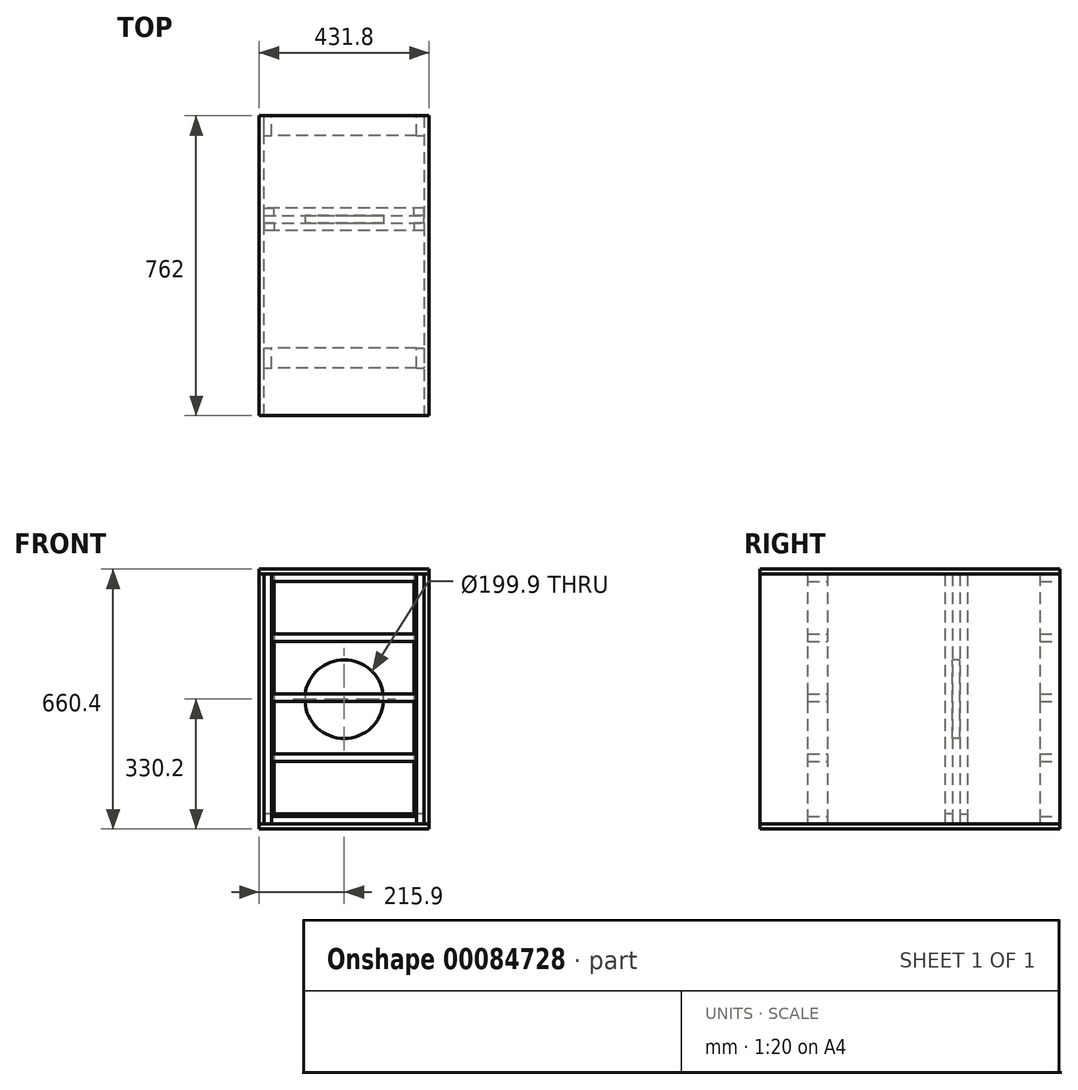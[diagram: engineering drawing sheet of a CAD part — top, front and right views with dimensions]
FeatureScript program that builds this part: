
annotation { "Feature Type Name" : "Feature", "Feature Type Description" : "" }
export const myFeature = defineFeature(function(context is Context, id is Id, definition is map)
    precondition{}
    {
        {
            var Q0;
            Q0=qCreatedBy(makeId("Front.planeOp"),FACE);
            var sketch = newSketch(context, id + "F0", { "sketchPlane" : qUnion([Q0])});
            skLineSegment(sketch, "E0.bottom", {"start": v(-203.2, 317.5) * mm, "end": v(203.2, 317.5) * mm});
            skLineSegment(sketch, "E0.top", {"start": v(-203.2, -317.5) * mm, "end": v(203.2, -317.5) * mm});
            skLineSegment(sketch, "E0.left", {"start": v(-203.2, 317.5) * mm, "end": v(-203.2, -317.5) * mm});
            skLineSegment(sketch, "E0.right", {"start": v(203.2, 317.5) * mm, "end": v(203.2, -317.5) * mm});
            skSolve(sketch);
        }
        {
            var Q0;
            Q0=makeQuery(id+"F0.imprint","IMPRINT",FACE,{"disambiguationData":[TD([[makeQuery(id+"F0.imprint","IMPRINT",EDGE,{"derivedFrom":sQuery(id+"F0.wireOp",EDGE,"E0.bottom")}),-1.0]])]});
            extrude(context, id + "F1", {"entities" : qUnion([Q0]), "depth" : 19.05 * mm});
        }
        {
            var Q0;
            Q0=makeQuery(id+"F1.opExtrude","CAP_FACE",FACE,{"disambiguationData":[OSD([sQuery(id+"F0.wireOp",EDGE,"E0.bottom"),sQuery(id+"F0.wireOp",EDGE,"E0.top"),sQuery(id+"F0.wireOp",EDGE,"E0.left"),sQuery(id+"F0.wireOp",EDGE,"E0.right")])],"isStart":false});
            var sketch = newSketch(context, id + "F2", { "sketchPlane" : qUnion([Q0])});
            skCircle(sketch, "E1", {"center": v(0, 0) * mm, "radius": 166.5 * mm});
            skSolve(sketch);
        }
        {
            var Q0;
            Q0=makeQuery(id+"F2.imprint","IMPRINT",FACE,{"disambiguationData":[TD([[makeQuery(id+"F2.imprint","IMPRINT",EDGE,{"derivedFrom":sQuery(id+"F2.wireOp",EDGE,"E1")}),-1.0]])]});
            var sketch = newSketch(context, id + "F3", { "sketchPlane" : qUnion([Q0])});
            skCircle(sketch, "E2", {"center": v(0, 0) * mm, "radius": 99.95 * mm});
            skSolve(sketch);
        }
        {
            var Q0;
            Q0=makeQuery(id+"F3.imprint","IMPRINT",FACE,{"disambiguationData":[TD([[makeQuery(id+"F3.imprint","IMPRINT",EDGE,{"derivedFrom":sQuery(id+"F3.wireOp",EDGE,"E2")}),1.0]])]});
            extrude(context, id + "F4", {"entities" : qUnion([Q0]), "operationType" : NewBodyOperationType.REMOVE, "endBound" : BoundingType.UP_TO_NEXT, "oppositeDirection" : true, "depth" : 25.4 * mm});
        }
        {
            var Q0;
            Q0=makeQuery(id+"F1.opExtrude","SWEPT_FACE",FACE,{"disambiguationData":[OSD([sQuery(id+"F0.wireOp",EDGE,"E0.top")])]});
            var sketch = newSketch(context, id + "F5", { "sketchPlane" : qUnion([Q0])});
            skLineSegment(sketch, "E3.bottom", {"start": v(203.2, -254) * mm, "end": v(215.9, -254) * mm});
            skLineSegment(sketch, "E3.top", {"start": v(203.2, 508) * mm, "end": v(215.9, 508) * mm});
            skLineSegment(sketch, "E3.left", {"start": v(203.2, -254) * mm, "end": v(203.2, 508) * mm});
            skLineSegment(sketch, "E3.right", {"start": v(215.9, -254) * mm, "end": v(215.9, 508) * mm});
            skLineSegment(sketch, "E4.bottom", {"start": v(-215.9, 508) * mm, "end": v(-203.2, 508) * mm});
            skLineSegment(sketch, "E4.top", {"start": v(-215.9, -254) * mm, "end": v(-203.2, -254) * mm});
            skLineSegment(sketch, "E4.left", {"start": v(-215.9, 508) * mm, "end": v(-215.9, -254) * mm});
            skLineSegment(sketch, "E4.right", {"start": v(-203.2, 508) * mm, "end": v(-203.2, -254) * mm});
            skSolve(sketch);
        }
        {
            var Q0;
            {var subQ3=sQuery(id+"F5.wireOp",EDGE,"E4.bottom");Q0=makeQuery(id+"F5.imprint","IMPRINT",FACE,{"disambiguationData":[TD([[makeQuery(id+"F5.imprint","IMPRINT",EDGE,{"derivedFrom":subQ3}),-1.0]])]});}
            var Q1;
            {var subQ4=sQuery(id+"F5.wireOp",EDGE,"E3.bottom");Q1=makeQuery(id+"F5.imprint","IMPRINT",FACE,{"disambiguationData":[TD([[makeQuery(id+"F5.imprint","IMPRINT",EDGE,{"derivedFrom":subQ4}),1.0]])]});}
            var Q2;
            Q2=makeQuery(id+"F1.opExtrude","SWEPT_FACE",FACE,{"disambiguationData":[OSD([sQuery(id+"F0.wireOp",EDGE,"E0.bottom")])]});
            extrude(context, id + "F6", {"entities" : qUnion([Q0, Q1]), "endBound" : BoundingType.UP_TO_SURFACE, "oppositeDirection" : true, "endBoundEntityFace" : qUnion([Q2]), "depth" : 19.05 * mm});
        }
        {
            var Q0;
            Q0=makeQuery(id+"F1.opExtrude","SWEPT_FACE",FACE,{"disambiguationData":[OSD([sQuery(id+"F0.wireOp",EDGE,"E0.top")])]});
            var sketch = newSketch(context, id + "F7", { "sketchPlane" : qUnion([Q0])});
            skLineSegment(sketch, "E5.bottom", {"start": v(-215.9, 508) * mm, "end": v(215.9, 508) * mm});
            skLineSegment(sketch, "E5.top", {"start": v(-215.9, -254) * mm, "end": v(215.9, -254) * mm});
            skLineSegment(sketch, "E5.left", {"start": v(-215.9, 508) * mm, "end": v(-215.9, -254) * mm});
            skLineSegment(sketch, "E5.right", {"start": v(215.9, 508) * mm, "end": v(215.9, -254) * mm});
            skSolve(sketch);
        }
        {
            var Q0;
            Q0=makeQuery(id+"F7.imprint","IMPRINT",FACE,{"disambiguationData":[TD([[makeQuery(id+"F7.imprint","IMPRINT",EDGE,{"derivedFrom":sQuery(id+"F7.wireOp",EDGE,"E5.bottom")}),-1.0]])]});
            var Q1;
            {var subQ0=sQuery(id+"F0.wireOp",EDGE,"E0.top");Q1=makeQuery(id+"F7.imprint","IMPRINT",FACE,{"disambiguationData":[TD([[makeQuery(id+"F7.imprint","IMPRINT",EDGE,{"derivedFrom":makeQuery(id+"F1.opExtrude","CAP_EDGE",EDGE,{"disambiguationData":[OSD([subQ0])],"isStart":true})}),1.0]])]});}
            extrude(context, id + "F8", {"entities" : qUnion([Q0, Q1]), "depth" : 12.7 * mm});
        }
        {
            var Q0;
            Q0=makeQuery(id+"F8.opExtrude","CAP_FACE",FACE,{"disambiguationData":[OSD([sQuery(id+"F7.wireOp",EDGE,"E5.bottom"),sQuery(id+"F7.wireOp",EDGE,"E5.top"),sQuery(id+"F7.wireOp",EDGE,"E5.left"),sQuery(id+"F7.wireOp",EDGE,"E5.right")])],"isStart":true});
            var sketch = newSketch(context, id + "F9", { "sketchPlane" : qUnion([Q0])});
            skLineSegment(sketch, "E6.bottom", {"start": v(-203.2, -387.35) * mm, "end": v(-184.15, -387.35) * mm});
            skLineSegment(sketch, "E6.top", {"start": v(-203.2, -336.55) * mm, "end": v(-184.15, -336.55) * mm});
            skLineSegment(sketch, "E6.left", {"start": v(-203.2, -387.35) * mm, "end": v(-203.2, -336.55) * mm});
            skLineSegment(sketch, "E6.right", {"start": v(-184.15, -387.35) * mm, "end": v(-184.15, -336.55) * mm});
            skLineSegment(sketch, "E7.bottom", {"start": v(184.15, -336.55) * mm, "end": v(203.2, -336.55) * mm});
            skLineSegment(sketch, "E7.top", {"start": v(184.15, -387.35) * mm, "end": v(203.2, -387.35) * mm});
            skLineSegment(sketch, "E7.left", {"start": v(184.15, -336.55) * mm, "end": v(184.15, -387.35) * mm});
            skLineSegment(sketch, "E7.right", {"start": v(203.2, -336.55) * mm, "end": v(203.2, -387.35) * mm});
            skSolve(sketch);
        }
        {
            var Q0;
            Q0=makeQuery(id+"F9.imprint","IMPRINT",FACE,{"disambiguationData":[TD([[makeQuery(id+"F9.imprint","IMPRINT",EDGE,{"derivedFrom":sQuery(id+"F9.wireOp",EDGE,"E6.bottom")}),1.0]])]});
            var Q1;
            Q1=makeQuery(id+"F9.imprint","IMPRINT",FACE,{"disambiguationData":[TD([[makeQuery(id+"F9.imprint","IMPRINT",EDGE,{"derivedFrom":sQuery(id+"F9.wireOp",EDGE,"E7.bottom")}),-1.0]])]});
            var Q2;
            Q2=makeQuery(id+"F6.opExtrude","CAP_FACE",FACE,{"disambiguationData":[OSD([sQuery(id+"F5.wireOp",EDGE,"E3.bottom"),sQuery(id+"F5.wireOp",EDGE,"E3.top"),sQuery(id+"F5.wireOp",EDGE,"E3.left"),sQuery(id+"F5.wireOp",EDGE,"E3.right")])],"isStart":false});
            extrude(context, id + "F10", {"entities" : qUnion([Q0, Q1]), "endBound" : BoundingType.UP_TO_SURFACE, "endBoundEntityFace" : qUnion([Q2]), "depth" : 19.05 * mm});
        }
        {
            var Q0;
            Q0=makeQuery(id+"F10.opExtrude","SWEPT_FACE",FACE,{"disambiguationData":[OSD([sQuery(id+"F9.wireOp",EDGE,"E6.right")])]});
            var sketch = newSketch(context, id + "F11", { "sketchPlane" : qUnion([Q0])});
            skLineSegment(sketch, "E8.bottom", {"start": v(-387.35, 317.5) * mm, "end": v(-336.55, 317.5) * mm});
            skLineSegment(sketch, "E8.top", {"start": v(-387.35, 298.45) * mm, "end": v(-336.55, 298.45) * mm});
            skLineSegment(sketch, "E8.left", {"start": v(-387.35, 317.5) * mm, "end": v(-387.35, 298.45) * mm});
            skLineSegment(sketch, "E8.right", {"start": v(-336.55, 317.5) * mm, "end": v(-336.55, 298.45) * mm});
            skLineSegment(sketch, "E9.bottom", {"start": v(-387.35, -298.45) * mm, "end": v(-336.55, -298.45) * mm});
            skLineSegment(sketch, "E9.top", {"start": v(-387.35, -317.5) * mm, "end": v(-336.55, -317.5) * mm});
            skLineSegment(sketch, "E9.left", {"start": v(-387.35, -298.45) * mm, "end": v(-387.35, -317.5) * mm});
            skLineSegment(sketch, "E9.right", {"start": v(-336.55, -298.45) * mm, "end": v(-336.55, -317.5) * mm});
            skLineSegment(sketch, "E10.bottom", {"start": v(-387.35, 165.1) * mm, "end": v(-336.55, 165.1) * mm});
            skLineSegment(sketch, "E10.top", {"start": v(-387.35, 146.05) * mm, "end": v(-336.55, 146.05) * mm});
            skLineSegment(sketch, "E10.left", {"start": v(-387.35, 165.1) * mm, "end": v(-387.35, 146.05) * mm});
            skLineSegment(sketch, "E10.right", {"start": v(-336.55, 165.1) * mm, "end": v(-336.55, 146.05) * mm});
            skLineSegment(sketch, "E11.bottom", {"start": v(-387.35, 12.7) * mm, "end": v(-336.55, 12.7) * mm});
            skLineSegment(sketch, "E11.top", {"start": v(-387.35, -6.35) * mm, "end": v(-336.55, -6.35) * mm});
            skLineSegment(sketch, "E11.left", {"start": v(-387.35, 12.7) * mm, "end": v(-387.35, -6.35) * mm});
            skLineSegment(sketch, "E11.right", {"start": v(-336.55, 12.7) * mm, "end": v(-336.55, -6.35) * mm});
            skLineSegment(sketch, "E12.bottom", {"start": v(-387.35, -139.7) * mm, "end": v(-336.55, -139.7) * mm});
            skLineSegment(sketch, "E12.top", {"start": v(-387.35, -158.75) * mm, "end": v(-336.55, -158.75) * mm});
            skLineSegment(sketch, "E12.left", {"start": v(-387.35, -139.7) * mm, "end": v(-387.35, -158.75) * mm});
            skLineSegment(sketch, "E12.right", {"start": v(-336.55, -139.7) * mm, "end": v(-336.55, -158.75) * mm});
            skSolve(sketch);
        }
        {
            var Q0;
            Q0=makeQuery(id+"F11.imprint","IMPRINT",FACE,{"disambiguationData":[TD([[makeQuery(id+"F11.imprint","IMPRINT",EDGE,{"derivedFrom":sQuery(id+"F11.wireOp",EDGE,"E8.bottom")}),-1.0]])]});
            var Q1;
            Q1=makeQuery(id+"F11.imprint","IMPRINT",FACE,{"disambiguationData":[TD([[makeQuery(id+"F11.imprint","IMPRINT",EDGE,{"derivedFrom":sQuery(id+"F11.wireOp",EDGE,"E9.bottom")}),-1.0]])]});
            var Q2;
            {var subQ0=sQuery(id+"F11.wireOp",EDGE,"E10.left");Q2=makeQuery(id+"F11.imprint","IMPRINT",FACE,{"disambiguationData":[TD([[makeQuery(id+"F11.imprint","IMPRINT",EDGE,{"derivedFrom":subQ0}),1.0]])]});}
            var Q3;
            {var subQ0=sQuery(id+"F11.wireOp",EDGE,"E11.left");Q3=makeQuery(id+"F11.imprint","IMPRINT",FACE,{"disambiguationData":[TD([[makeQuery(id+"F11.imprint","IMPRINT",EDGE,{"derivedFrom":subQ0}),1.0]])]});}
            var Q4;
            {var subQ0=sQuery(id+"F11.wireOp",EDGE,"E12.right");Q4=makeQuery(id+"F11.imprint","IMPRINT",FACE,{"disambiguationData":[TD([[makeQuery(id+"F11.imprint","IMPRINT",EDGE,{"derivedFrom":subQ0}),-1.0]])]});}
            extrude(context, id + "F12", {"entities" : qUnion([Q0, Q1, Q2, Q3, Q4]), "endBound" : BoundingType.UP_TO_NEXT, "depth" : 25.4 * mm});
        }
        {
            var Q0;
            Q0=makeQuery(id+"F6.opExtrude","CAP_FACE",FACE,{"disambiguationData":[OSD([sQuery(id+"F5.wireOp",EDGE,"E4.bottom"),sQuery(id+"F5.wireOp",EDGE,"E4.top"),sQuery(id+"F5.wireOp",EDGE,"E4.left"),sQuery(id+"F5.wireOp",EDGE,"E4.right")])],"isStart":false});
            var sketch = newSketch(context, id + "F13", { "sketchPlane" : qUnion([Q0])});
            skLineSegment(sketch, "E13.bottom", {"start": v(-215.9, -508) * mm, "end": v(215.9, -508) * mm});
            skLineSegment(sketch, "E13.top", {"start": v(-215.9, 254) * mm, "end": v(215.9, 254) * mm});
            skLineSegment(sketch, "E13.left", {"start": v(-215.9, -508) * mm, "end": v(-215.9, 254) * mm});
            skLineSegment(sketch, "E13.right", {"start": v(215.9, -508) * mm, "end": v(215.9, 254) * mm});
            skSolve(sketch);
        }
        {
            var Q0;
            {var subQ2=sQuery(id+"F13.wireOp",EDGE,"E13.right");Q0=makeQuery(id+"F13.imprint","IMPRINT",FACE,{"disambiguationData":[TD([[makeQuery(id+"F13.imprint","IMPRINT",EDGE,{"derivedFrom":subQ2}),1.0]])]});}
            var Q1;
            {var subQ0=sQuery(id+"F13.wireOp",EDGE,"E13.left");Q1=makeQuery(id+"F13.imprint","IMPRINT",FACE,{"disambiguationData":[TD([[makeQuery(id+"F13.imprint","IMPRINT",EDGE,{"derivedFrom":subQ0}),-1.0]])]});}
            extrude(context, id + "F14", {"entities" : qUnion([Q0, Q1]), "depth" : 12.7 * mm});
        }
        {
            var Q0;
            Q0=makeQuery(id+"F8.opExtrude","CAP_FACE",FACE,{"disambiguationData":[OSD([sQuery(id+"F7.wireOp",EDGE,"E5.bottom"),sQuery(id+"F7.wireOp",EDGE,"E5.top"),sQuery(id+"F7.wireOp",EDGE,"E5.left"),sQuery(id+"F7.wireOp",EDGE,"E5.right")])],"isStart":true});
            var sketch = newSketch(context, id + "F15", { "sketchPlane" : qUnion([Q0])});
            skLineSegment(sketch, "E14.bottom", {"start": v(203.2, -19.05) * mm, "end": v(-203.2, -19.05) * mm});
            skLineSegment(sketch, "E14.top", {"start": v(203.2, -38.1) * mm, "end": v(-203.2, -38.1) * mm});
            skLineSegment(sketch, "E14.left", {"start": v(203.2, -19.05) * mm, "end": v(203.2, -38.1) * mm});
            skLineSegment(sketch, "E14.right", {"start": v(-203.2, -19.05) * mm, "end": v(-203.2, -38.1) * mm});
            skLineSegment(sketch, "E15.bottom", {"start": v(203.2, 19.05) * mm, "end": v(-203.2, 19.05) * mm});
            skLineSegment(sketch, "E15.top", {"start": v(203.2, 0) * mm, "end": v(-203.2, 0) * mm});
            skLineSegment(sketch, "E15.left", {"start": v(203.2, 19.05) * mm, "end": v(203.2, 0) * mm});
            skLineSegment(sketch, "E15.right", {"start": v(-203.2, 19.05) * mm, "end": v(-203.2, 0) * mm});
            skSolve(sketch);
        }
        {
            var Q0;
            Q0=makeQuery(id+"F15.imprint","IMPRINT",FACE,{"disambiguationData":[TD([[makeQuery(id+"F15.imprint","IMPRINT",EDGE,{"derivedFrom":sQuery(id+"F15.wireOp",EDGE,"E15.bottom")}),1.0]])]});
            var Q1;
            Q1=makeQuery(id+"F15.imprint","IMPRINT",FACE,{"disambiguationData":[TD([[makeQuery(id+"F15.imprint","IMPRINT",EDGE,{"derivedFrom":sQuery(id+"F15.wireOp",EDGE,"E14.bottom")}),1.0]])]});
            extrude(context, id + "F16", {"entities" : qUnion([Q0, Q1]), "depth" : 25.4 * mm});
        }
        {
            var Q0;
            Q0=makeQuery(id+"F16.opExtrude","CAP_FACE",FACE,{"disambiguationData":[OSD([sQuery(id+"F15.wireOp",EDGE,"E14.bottom"),sQuery(id+"F15.wireOp",EDGE,"E14.top"),sQuery(id+"F15.wireOp",EDGE,"E14.left"),sQuery(id+"F15.wireOp",EDGE,"E14.right")])],"isStart":false});
            var sketch = newSketch(context, id + "F17", { "sketchPlane" : qUnion([Q0])});
            skLineSegment(sketch, "E16.bottom", {"start": v(203.2, -19.05) * mm, "end": v(177.8, -19.05) * mm});
            skLineSegment(sketch, "E16.top", {"start": v(203.2, -38.1) * mm, "end": v(177.8, -38.1) * mm});
            skLineSegment(sketch, "E16.left", {"start": v(203.2, -19.05) * mm, "end": v(203.2, -38.1) * mm});
            skLineSegment(sketch, "E16.right", {"start": v(177.8, -19.05) * mm, "end": v(177.8, -38.1) * mm});
            skLineSegment(sketch, "E17.bottom", {"start": v(203.2, 0) * mm, "end": v(177.8, 0) * mm});
            skLineSegment(sketch, "E17.top", {"start": v(203.2, 19.05) * mm, "end": v(177.8, 19.05) * mm});
            skLineSegment(sketch, "E17.left", {"start": v(203.2, 0) * mm, "end": v(203.2, 19.05) * mm});
            skLineSegment(sketch, "E17.right", {"start": v(177.8, 0) * mm, "end": v(177.8, 19.05) * mm});
            skLineSegment(sketch, "E18.bottom", {"start": v(-203.2, -19.05) * mm, "end": v(-177.8, -19.05) * mm});
            skLineSegment(sketch, "E18.top", {"start": v(-203.2, -38.1) * mm, "end": v(-177.8, -38.1) * mm});
            skLineSegment(sketch, "E18.left", {"start": v(-203.2, -19.05) * mm, "end": v(-203.2, -38.1) * mm});
            skLineSegment(sketch, "E18.right", {"start": v(-177.8, -19.05) * mm, "end": v(-177.8, -38.1) * mm});
            skLineSegment(sketch, "E19.bottom", {"start": v(-203.2, 0) * mm, "end": v(-177.8, 0) * mm});
            skLineSegment(sketch, "E19.top", {"start": v(-203.2, 19.05) * mm, "end": v(-177.8, 19.05) * mm});
            skLineSegment(sketch, "E19.left", {"start": v(-203.2, 0) * mm, "end": v(-203.2, 19.05) * mm});
            skLineSegment(sketch, "E19.right", {"start": v(-177.8, 0) * mm, "end": v(-177.8, 19.05) * mm});
            skSolve(sketch);
        }
        {
            var Q0;
            Q0=makeQuery(id+"F17.imprint","IMPRINT",FACE,{"disambiguationData":[TD([[makeQuery(id+"F17.imprint","IMPRINT",EDGE,{"derivedFrom":sQuery(id+"F17.wireOp",EDGE,"E17.bottom")}),-1.0]])]});
            var Q1;
            Q1=makeQuery(id+"F17.imprint","IMPRINT",FACE,{"disambiguationData":[TD([[makeQuery(id+"F17.imprint","IMPRINT",EDGE,{"derivedFrom":sQuery(id+"F17.wireOp",EDGE,"E16.bottom")}),1.0]])]});
            var Q2;
            Q2=makeQuery(id+"F17.imprint","IMPRINT",FACE,{"disambiguationData":[TD([[makeQuery(id+"F17.imprint","IMPRINT",EDGE,{"derivedFrom":sQuery(id+"F17.wireOp",EDGE,"E18.bottom")}),1.0]])]});
            var Q3;
            Q3=makeQuery(id+"F17.imprint","IMPRINT",FACE,{"disambiguationData":[TD([[makeQuery(id+"F17.imprint","IMPRINT",EDGE,{"derivedFrom":sQuery(id+"F17.wireOp",EDGE,"E19.bottom")}),1.0]])]});
            extrude(context, id + "F18", {"entities" : qUnion([Q0, Q1, Q2, Q3]), "endBound" : BoundingType.UP_TO_NEXT, "depth" : 25.4 * mm});
        }
        {
            var Q0;
            Q0=makeQuery(id+"F12.opExtrude","SWEPT_BODY",BODY,{"disambiguationData":[OSD([sQuery(id+"F11.wireOp",EDGE,"E8.bottom"),sQuery(id+"F11.wireOp",EDGE,"E8.top"),sQuery(id+"F11.wireOp",EDGE,"E8.left"),sQuery(id+"F11.wireOp",EDGE,"E8.right")])]});
            var Q1;
            Q1=makeQuery(id+"F12.opExtrude","SWEPT_BODY",BODY,{"disambiguationData":[OSD([sQuery(id+"F11.wireOp",EDGE,"E10.bottom"),sQuery(id+"F11.wireOp",EDGE,"E10.top"),sQuery(id+"F11.wireOp",EDGE,"E10.left"),sQuery(id+"F11.wireOp",EDGE,"E10.right")])]});
            var Q2;
            Q2=makeQuery(id+"F12.opExtrude","SWEPT_BODY",BODY,{"disambiguationData":[OSD([sQuery(id+"F11.wireOp",EDGE,"E11.bottom"),sQuery(id+"F11.wireOp",EDGE,"E11.top"),sQuery(id+"F11.wireOp",EDGE,"E11.left"),sQuery(id+"F11.wireOp",EDGE,"E11.right")])]});
            var Q3;
            Q3=makeQuery(id+"F12.opExtrude","SWEPT_BODY",BODY,{"disambiguationData":[OSD([sQuery(id+"F11.wireOp",EDGE,"E12.bottom"),sQuery(id+"F11.wireOp",EDGE,"E12.top"),sQuery(id+"F11.wireOp",EDGE,"E12.left"),sQuery(id+"F11.wireOp",EDGE,"E12.right")])]});
            var Q4;
            Q4=makeQuery(id+"F12.opExtrude","SWEPT_BODY",BODY,{"disambiguationData":[OSD([sQuery(id+"F11.wireOp",EDGE,"E9.bottom"),sQuery(id+"F11.wireOp",EDGE,"E9.top"),sQuery(id+"F11.wireOp",EDGE,"E9.left"),sQuery(id+"F11.wireOp",EDGE,"E9.right")])]});
            var Q5;
            Q5=makeQuery(id+"F10.opExtrude","SWEPT_BODY",BODY,{"disambiguationData":[OSD([sQuery(id+"F9.wireOp",EDGE,"E6.bottom"),sQuery(id+"F9.wireOp",EDGE,"E6.top"),sQuery(id+"F9.wireOp",EDGE,"E6.left"),sQuery(id+"F9.wireOp",EDGE,"E6.right")])]});
            var Q6;
            Q6=makeQuery(id+"F10.opExtrude","SWEPT_BODY",BODY,{"disambiguationData":[OSD([sQuery(id+"F9.wireOp",EDGE,"E7.bottom"),sQuery(id+"F9.wireOp",EDGE,"E7.top"),sQuery(id+"F9.wireOp",EDGE,"E7.left"),sQuery(id+"F9.wireOp",EDGE,"E7.right")])]});
            var Q7;
            Q7=makeQuery(id+"F6.opExtrude","CAP_EDGE",EDGE,{"disambiguationData":[OSD([sQuery(id+"F5.wireOp",EDGE,"E3.left")])],"isStart":false});
            transform(context, id + "F19", {"entities" : qUnion([Q0, Q1, Q2, Q3, Q4, Q5, Q6]), "transformType" : TransformType.TRANSLATION_DISTANCE, "transformDirection" : qUnion([Q7]), "distance" : 590.55 * mm, "oppositeDirection" : true, "makeCopy" : true});
        }
    });
